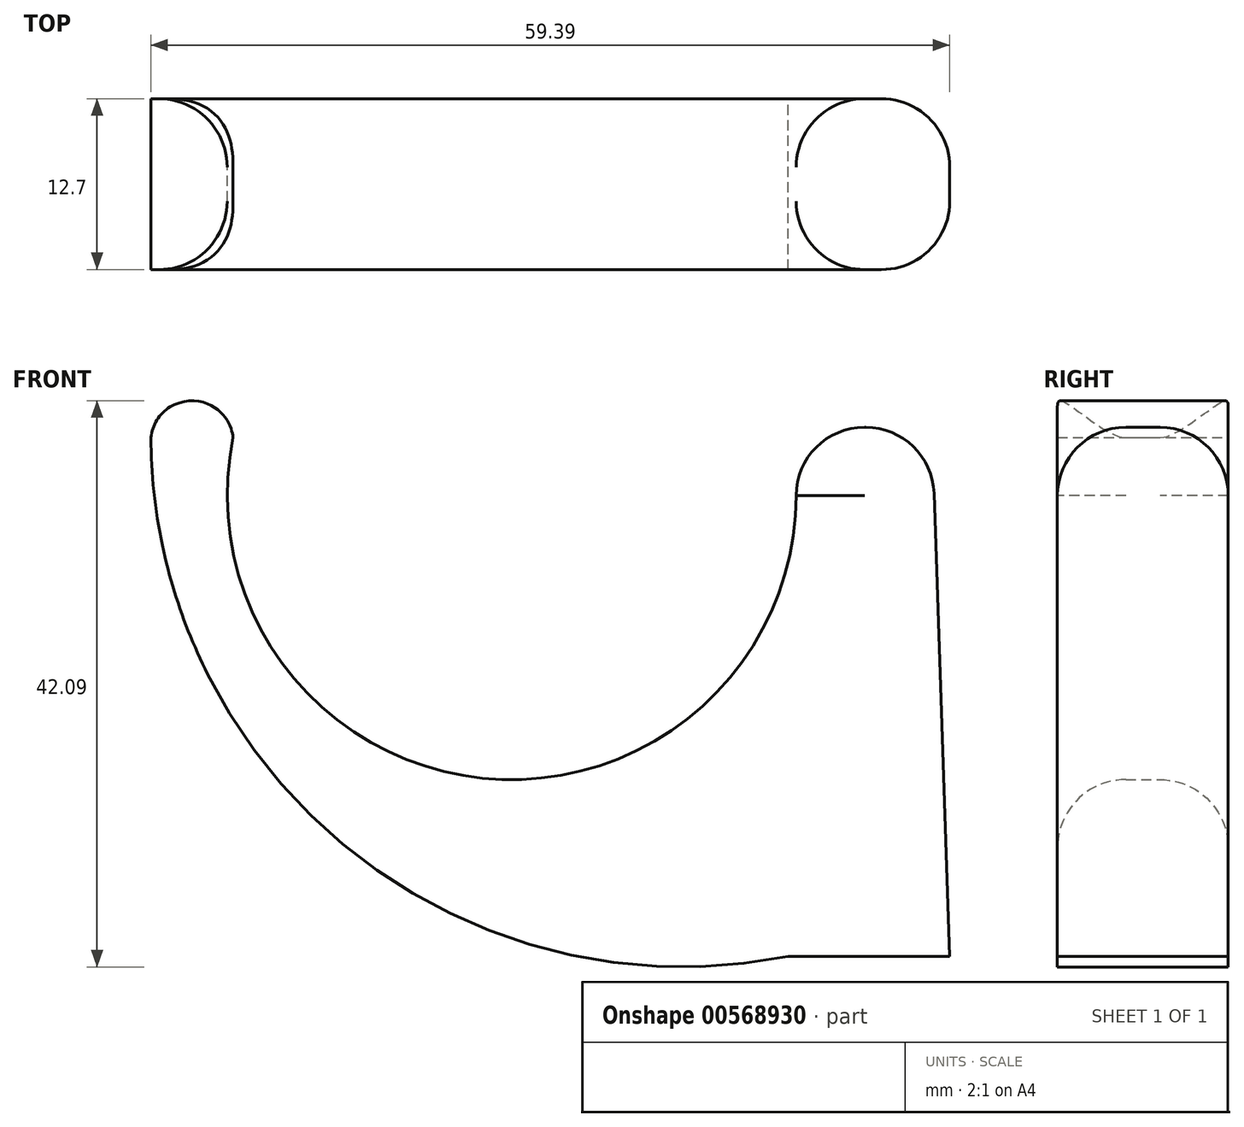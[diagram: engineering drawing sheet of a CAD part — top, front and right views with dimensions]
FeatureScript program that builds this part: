
annotation { "Feature Type Name" : "Feature", "Feature Type Description" : "" }
export const myFeature = defineFeature(function(context is Context, id is Id, definition is map)
    precondition{}
    {
        {
            var Q0;
            Q0=qCreatedBy(makeId("Front.planeOp"),FACE);
            var sketch = newSketch(context, id + "F0", { "sketchPlane" : qUnion([Q0])});
            skArc(sketch, "E0", {"start": v(-34.85, 23.77) * mm, "mid": v(-13.75, -1.65) * mm, "end": v(6.4, 24.54) * mm});
            skArc(sketch, "E1", {"start": v(-34.85, 23.77) * mm, "mid": v(-37.9, 26.52) * mm, "end": v(-40.96, 23.77) * mm});
            skArc(sketch, "E2", {"start": v(-40.96, 23.77) * mm, "mid": v(-26.4, -6.7) * mm, "end": v(6.4, -14.8) * mm});
            skLineSegment(sketch, "E3", {"start": v(6.4, 24.54) * mm, "end": v(17.1, 24.54) * mm});
            skLineSegment(sketch, "E4", {"start": v(17.1, 24.54) * mm, "end": v(18.43, -14.8) * mm});
            skLineSegment(sketch, "E5", {"start": v(18.43, -14.8) * mm, "end": v(6.4, -14.8) * mm});
            skSolve(sketch);
        }
        {
            var Q0;
            Q0=makeQuery(id+"F0.imprint","IMPRINT",FACE,{"disambiguationData":[TD([[makeQuery(id+"F0.imprint","IMPRINT",EDGE,{"derivedFrom":sQuery(id+"F0.wireOp",EDGE,"E0")}),-1.0]])]});
            extrude(context, id + "F1", {"entities" : qUnion([Q0]), "depth" : 12.7 * mm, "offsetDistance" : 25.4 * mm});
        }
        {
            var Q0;
            Q0=makeQuery(id+"F1.opExtrude","CAP_EDGE",EDGE,{"disambiguationData":[OSD([sQuery(id+"F0.wireOp",EDGE,"E3")])],"isStart":false});
            var Q1;
            Q1=makeQuery(id+"F1.opExtrude","CAP_EDGE",EDGE,{"disambiguationData":[OSD([sQuery(id+"F0.wireOp",EDGE,"E3")])],"isStart":true});
            var Q2;
            Q2=makeQuery(id+"F1.opExtrude","SWEPT_EDGE",EDGE,{"disambiguationData":[OSD([sQuery(id+"F0.wireOp",EDGE,"E3"),sQuery(id+"F0.wireOp",EDGE,"E4")])]});
            var Q3;
            Q3=makeQuery(id+"F1.opExtrude","SWEPT_EDGE",EDGE,{"disambiguationData":[OSD([sQuery(id+"F0.wireOp",EDGE,"E0"),sQuery(id+"F0.wireOp",EDGE,"E3")])]});
            var Q4;
            Q4=makeQuery(id+"F1.opExtrude","CAP_EDGE",EDGE,{"disambiguationData":[OSD([sQuery(id+"F0.wireOp",EDGE,"E4")])],"isStart":false});
            var Q5;
            Q5=makeQuery(id+"F1.opExtrude","CAP_EDGE",EDGE,{"disambiguationData":[OSD([sQuery(id+"F0.wireOp",EDGE,"E4")])],"isStart":true});
            var Q6;
            Q6=makeQuery(id+"F1.opExtrude","CAP_EDGE",EDGE,{"disambiguationData":[OSD([sQuery(id+"F0.wireOp",EDGE,"E0")])],"isStart":true});
            var Q7;
            Q7=makeQuery(id+"F1.opExtrude","CAP_EDGE",EDGE,{"disambiguationData":[OSD([sQuery(id+"F0.wireOp",EDGE,"E0")])],"isStart":false});
            fillet(context, id + "F2", {"entities" : qUnion([Q0, Q1, Q2, Q3, Q4, Q5, Q6, Q7]), "radius" : 5.08 * mm, "tangentPropagation" : true, "allowEdgeOverflow" : false});
        }
    });
